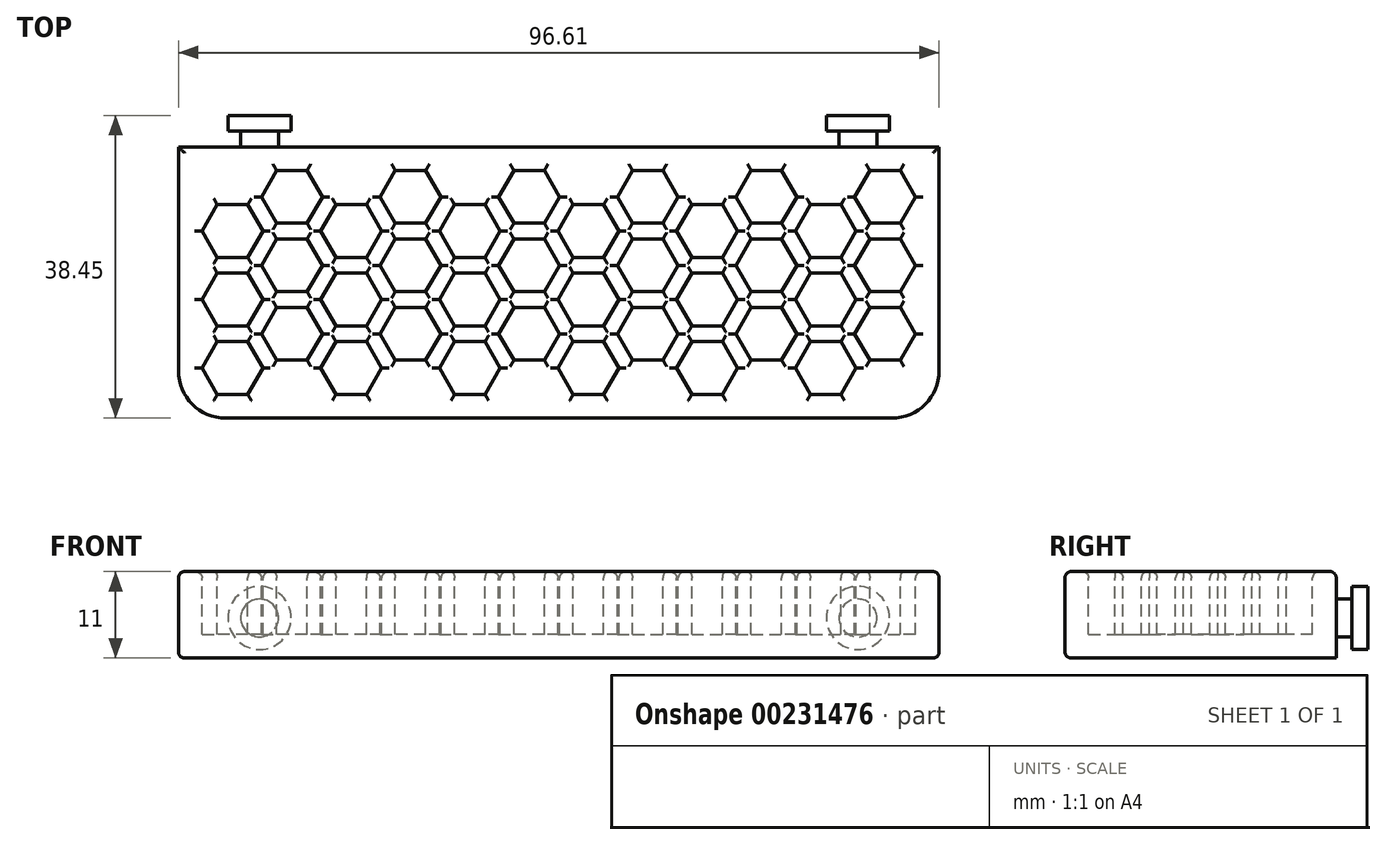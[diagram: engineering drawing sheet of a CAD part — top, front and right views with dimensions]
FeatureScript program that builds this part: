
annotation { "Feature Type Name" : "Feature", "Feature Type Description" : "" }
export const myFeature = defineFeature(function(context is Context, id is Id, definition is map)
    precondition{}
    {
        {
            var Q0;
            Q0=qCreatedBy(makeId("Top.planeOp"),FACE);
            var sketch = newSketch(context, id + "F0", { "sketchPlane" : qUnion([Q0])});
            skCircle(sketch, "E0.cCircle", {"center": v(0, 0) * mm, "radius": 3.35 * mm, "construction": true});
            skLineSegment(sketch, "E0.0", {"start": v(1.93, -3.35) * mm, "end": v(-1.93, -3.35) * mm, "construction": true});
            skLineSegment(sketch, "E0.1", {"start": v(-1.93, -3.35) * mm, "end": v(-3.87, 0) * mm, "construction": true});
            skLineSegment(sketch, "E0.2", {"start": v(-3.87, 0) * mm, "end": v(-1.93, 3.35) * mm, "construction": true});
            skLineSegment(sketch, "E0.3", {"start": v(-1.93, 3.35) * mm, "end": v(1.93, 3.35) * mm, "construction": true});
            skLineSegment(sketch, "E0.4", {"start": v(1.93, 3.35) * mm, "end": v(3.87, 0) * mm, "construction": true});
            skLineSegment(sketch, "E0.5", {"start": v(3.87, 0) * mm, "end": v(1.93, -3.35) * mm, "construction": true});
            skPoint(sketch, "E0.0.midPoint", {"position": v(0, -3.35) * mm});
            skLineSegment(sketch, "E1", {"start": v(1.18, 6.66) * mm, "end": v(5.6, -1) * mm, "construction": true});
            skPoint(sketch, "E2", {"position": v(7.53, 4.35) * mm});
            skCircle(sketch, "E3.0.1.0", {"center": v(7.53, 4.35) * mm, "radius": 3.35 * mm, "construction": true});
            skLineSegment(sketch, "E3.0.1.1", {"start": v(3.67, 4.35) * mm, "end": v(5.6, 7.7) * mm, "construction": true});
            skLineSegment(sketch, "E3.0.1.2", {"start": v(9.47, 7.7) * mm, "end": v(11.4, 4.35) * mm, "construction": true});
            skLineSegment(sketch, "E3.0.1.3", {"start": v(11.4, 4.35) * mm, "end": v(9.47, 1) * mm, "construction": true});
            skPoint(sketch, "E3.0.1.4", {"position": v(7.53, 1) * mm});
            skLineSegment(sketch, "E3.0.1.5", {"start": v(5.6, 1) * mm, "end": v(3.67, 4.35) * mm, "construction": true});
            skLineSegment(sketch, "E3.0.1.6", {"start": v(9.47, 1) * mm, "end": v(5.6, 1) * mm, "construction": true});
            skLineSegment(sketch, "E3.0.1.7", {"start": v(5.6, 7.7) * mm, "end": v(9.47, 7.7) * mm, "construction": true});
            skCircle(sketch, "E3.0.2.0", {"center": v(15.07, 8.7) * mm, "radius": 3.35 * mm, "construction": true});
            skLineSegment(sketch, "E3.0.2.1", {"start": v(11.2, 8.7) * mm, "end": v(13.13, 12.05) * mm, "construction": true});
            skLineSegment(sketch, "E3.0.2.2", {"start": v(17, 12.05) * mm, "end": v(18.94, 8.7) * mm, "construction": true});
            skLineSegment(sketch, "E3.0.2.3", {"start": v(18.94, 8.7) * mm, "end": v(17, 5.35) * mm, "construction": true});
            skPoint(sketch, "E3.0.2.4", {"position": v(15.07, 5.35) * mm});
            skLineSegment(sketch, "E3.0.2.5", {"start": v(13.13, 5.35) * mm, "end": v(11.2, 8.7) * mm, "construction": true});
            skLineSegment(sketch, "E3.0.2.6", {"start": v(17, 5.35) * mm, "end": v(13.13, 5.35) * mm, "construction": true});
            skLineSegment(sketch, "E3.0.2.7", {"start": v(13.13, 12.05) * mm, "end": v(17, 12.05) * mm, "construction": true});
            skCircle(sketch, "E3.1.0.0", {"center": v(15.07, 0) * mm, "radius": 3.35 * mm, "construction": true});
            skLineSegment(sketch, "E3.1.0.1", {"start": v(11.2, 0) * mm, "end": v(13.13, 3.35) * mm, "construction": true});
            skLineSegment(sketch, "E3.1.0.2", {"start": v(17, 3.35) * mm, "end": v(18.94, 0) * mm, "construction": true});
            skLineSegment(sketch, "E3.1.0.3", {"start": v(18.94, 0) * mm, "end": v(17, -3.35) * mm, "construction": true});
            skPoint(sketch, "E3.1.0.4", {"position": v(15.07, -3.35) * mm});
            skLineSegment(sketch, "E3.1.0.5", {"start": v(13.13, -3.35) * mm, "end": v(11.2, 0) * mm, "construction": true});
            skLineSegment(sketch, "E3.1.0.6", {"start": v(17, -3.35) * mm, "end": v(13.13, -3.35) * mm, "construction": true});
            skLineSegment(sketch, "E3.1.0.7", {"start": v(13.13, 3.35) * mm, "end": v(17, 3.35) * mm, "construction": true});
            skCircle(sketch, "E3.1.1.0", {"center": v(22.6, 4.35) * mm, "radius": 3.35 * mm, "construction": true});
            skLineSegment(sketch, "E3.1.1.1", {"start": v(18.74, 4.35) * mm, "end": v(20.67, 7.7) * mm, "construction": true});
            skLineSegment(sketch, "E3.1.1.2", {"start": v(24.54, 7.7) * mm, "end": v(26.47, 4.35) * mm});
            skLineSegment(sketch, "E3.1.1.3", {"start": v(26.47, 4.35) * mm, "end": v(24.54, 1) * mm, "construction": true});
            skPoint(sketch, "E3.1.1.4", {"position": v(22.6, 1) * mm});
            skLineSegment(sketch, "E3.1.1.5", {"start": v(20.67, 1) * mm, "end": v(18.74, 4.35) * mm, "construction": true});
            skLineSegment(sketch, "E3.1.1.6", {"start": v(24.54, 1) * mm, "end": v(20.67, 1) * mm, "construction": true});
            skLineSegment(sketch, "E3.1.1.7", {"start": v(20.67, 7.7) * mm, "end": v(24.54, 7.7) * mm, "construction": true});
            skCircle(sketch, "E3.1.2.0", {"center": v(30.14, 8.7) * mm, "radius": 3.35 * mm, "construction": true});
            skLineSegment(sketch, "E3.1.2.1", {"start": v(26.27, 8.7) * mm, "end": v(28.2, 12.05) * mm});
            skLineSegment(sketch, "E3.1.2.2", {"start": v(32.07, 12.05) * mm, "end": v(34, 8.7) * mm});
            skLineSegment(sketch, "E3.1.2.3", {"start": v(34, 8.7) * mm, "end": v(32.07, 5.35) * mm});
            skPoint(sketch, "E3.1.2.4", {"position": v(30.14, 5.35) * mm});
            skLineSegment(sketch, "E3.1.2.5", {"start": v(28.2, 5.35) * mm, "end": v(26.27, 8.7) * mm});
            skLineSegment(sketch, "E3.1.2.6", {"start": v(32.07, 5.35) * mm, "end": v(28.2, 5.35) * mm});
            skLineSegment(sketch, "E3.1.2.7", {"start": v(28.2, 12.05) * mm, "end": v(32.07, 12.05) * mm});
            skCircle(sketch, "E3.2.0.0", {"center": v(30.14, 0) * mm, "radius": 3.35 * mm, "construction": true});
            skLineSegment(sketch, "E3.2.0.1", {"start": v(26.27, 0) * mm, "end": v(28.2, 3.35) * mm});
            skLineSegment(sketch, "E3.2.0.2", {"start": v(32.07, 3.35) * mm, "end": v(34, 0) * mm});
            skLineSegment(sketch, "E3.2.0.3", {"start": v(34, 0) * mm, "end": v(32.07, -3.35) * mm});
            skPoint(sketch, "E3.2.0.4", {"position": v(30.14, -3.35) * mm});
            skLineSegment(sketch, "E3.2.0.5", {"start": v(28.2, -3.35) * mm, "end": v(26.27, 0) * mm});
            skLineSegment(sketch, "E3.2.0.6", {"start": v(32.07, -3.35) * mm, "end": v(28.2, -3.35) * mm});
            skLineSegment(sketch, "E3.2.0.7", {"start": v(28.2, 3.35) * mm, "end": v(32.07, 3.35) * mm});
            skCircle(sketch, "E3.2.1.0", {"center": v(37.67, 4.35) * mm, "radius": 3.35 * mm, "construction": true});
            skLineSegment(sketch, "E3.2.1.1", {"start": v(33.8, 4.35) * mm, "end": v(35.74, 7.7) * mm});
            skLineSegment(sketch, "E3.2.1.2", {"start": v(39.6, 7.7) * mm, "end": v(41.54, 4.35) * mm});
            skLineSegment(sketch, "E3.2.1.3", {"start": v(41.54, 4.35) * mm, "end": v(39.6, 1) * mm});
            skPoint(sketch, "E3.2.1.4", {"position": v(37.67, 1) * mm});
            skLineSegment(sketch, "E3.2.1.5", {"start": v(35.74, 1) * mm, "end": v(33.8, 4.35) * mm});
            skLineSegment(sketch, "E3.2.1.6", {"start": v(39.6, 1) * mm, "end": v(35.74, 1) * mm});
            skLineSegment(sketch, "E3.2.1.7", {"start": v(35.74, 7.7) * mm, "end": v(39.6, 7.7) * mm});
            skCircle(sketch, "E3.2.2.0", {"center": v(45.2, 8.7) * mm, "radius": 3.35 * mm, "construction": true});
            skLineSegment(sketch, "E3.2.2.1", {"start": v(41.34, 8.7) * mm, "end": v(43.27, 12.05) * mm});
            skLineSegment(sketch, "E3.2.2.2", {"start": v(47.14, 12.05) * mm, "end": v(49.07, 8.7) * mm});
            skLineSegment(sketch, "E3.2.2.3", {"start": v(49.07, 8.7) * mm, "end": v(47.14, 5.35) * mm});
            skPoint(sketch, "E3.2.2.4", {"position": v(45.2, 5.35) * mm});
            skLineSegment(sketch, "E3.2.2.5", {"start": v(43.27, 5.35) * mm, "end": v(41.34, 8.7) * mm});
            skLineSegment(sketch, "E3.2.2.6", {"start": v(47.14, 5.35) * mm, "end": v(43.27, 5.35) * mm});
            skLineSegment(sketch, "E3.2.2.7", {"start": v(43.27, 12.05) * mm, "end": v(47.14, 12.05) * mm});
            skCircle(sketch, "E3.3.0.0", {"center": v(45.2, 0) * mm, "radius": 3.35 * mm, "construction": true});
            skLineSegment(sketch, "E3.3.0.1", {"start": v(41.34, 0) * mm, "end": v(43.27, 3.35) * mm});
            skLineSegment(sketch, "E3.3.0.2", {"start": v(47.14, 3.35) * mm, "end": v(49.07, 0) * mm});
            skLineSegment(sketch, "E3.3.0.3", {"start": v(49.07, 0) * mm, "end": v(47.14, -3.35) * mm});
            skPoint(sketch, "E3.3.0.4", {"position": v(45.2, -3.35) * mm});
            skLineSegment(sketch, "E3.3.0.5", {"start": v(43.27, -3.35) * mm, "end": v(41.34, 0) * mm});
            skLineSegment(sketch, "E3.3.0.6", {"start": v(47.14, -3.35) * mm, "end": v(43.27, -3.35) * mm});
            skLineSegment(sketch, "E3.3.0.7", {"start": v(43.27, 3.35) * mm, "end": v(47.14, 3.35) * mm});
            skCircle(sketch, "E3.3.1.0", {"center": v(52.74, 4.35) * mm, "radius": 3.35 * mm, "construction": true});
            skLineSegment(sketch, "E3.3.1.1", {"start": v(48.87, 4.35) * mm, "end": v(50.8, 7.7) * mm});
            skLineSegment(sketch, "E3.3.1.2", {"start": v(54.68, 7.7) * mm, "end": v(56.6, 4.35) * mm});
            skLineSegment(sketch, "E3.3.1.3", {"start": v(56.6, 4.35) * mm, "end": v(54.68, 1) * mm});
            skPoint(sketch, "E3.3.1.4", {"position": v(52.74, 1) * mm});
            skLineSegment(sketch, "E3.3.1.5", {"start": v(50.8, 1) * mm, "end": v(48.87, 4.35) * mm});
            skLineSegment(sketch, "E3.3.1.6", {"start": v(54.68, 1) * mm, "end": v(50.8, 1) * mm});
            skLineSegment(sketch, "E3.3.1.7", {"start": v(50.8, 7.7) * mm, "end": v(54.68, 7.7) * mm});
            skCircle(sketch, "E3.3.2.0", {"center": v(60.28, 8.7) * mm, "radius": 3.35 * mm, "construction": true});
            skLineSegment(sketch, "E3.3.2.1", {"start": v(56.4, 8.7) * mm, "end": v(58.34, 12.05) * mm});
            skLineSegment(sketch, "E3.3.2.2", {"start": v(62.2, 12.05) * mm, "end": v(64.14, 8.7) * mm});
            skLineSegment(sketch, "E3.3.2.3", {"start": v(64.14, 8.7) * mm, "end": v(62.2, 5.35) * mm});
            skPoint(sketch, "E3.3.2.4", {"position": v(60.28, 5.35) * mm});
            skLineSegment(sketch, "E3.3.2.5", {"start": v(58.34, 5.35) * mm, "end": v(56.4, 8.7) * mm});
            skLineSegment(sketch, "E3.3.2.6", {"start": v(62.2, 5.35) * mm, "end": v(58.34, 5.35) * mm});
            skLineSegment(sketch, "E3.3.2.7", {"start": v(58.34, 12.05) * mm, "end": v(62.2, 12.05) * mm});
            skCircle(sketch, "E3.4.0.0", {"center": v(60.28, 0) * mm, "radius": 3.35 * mm, "construction": true});
            skLineSegment(sketch, "E3.4.0.1", {"start": v(56.4, 0) * mm, "end": v(58.34, 3.35) * mm});
            skLineSegment(sketch, "E3.4.0.2", {"start": v(62.2, 3.35) * mm, "end": v(64.14, 0) * mm});
            skLineSegment(sketch, "E3.4.0.3", {"start": v(64.14, 0) * mm, "end": v(62.2, -3.35) * mm});
            skPoint(sketch, "E3.4.0.4", {"position": v(60.28, -3.35) * mm});
            skLineSegment(sketch, "E3.4.0.5", {"start": v(58.34, -3.35) * mm, "end": v(56.4, 0) * mm});
            skLineSegment(sketch, "E3.4.0.6", {"start": v(62.2, -3.35) * mm, "end": v(58.34, -3.35) * mm});
            skLineSegment(sketch, "E3.4.0.7", {"start": v(58.34, 3.35) * mm, "end": v(62.2, 3.35) * mm});
            skCircle(sketch, "E3.4.1.0", {"center": v(67.8, 4.35) * mm, "radius": 3.35 * mm, "construction": true});
            skLineSegment(sketch, "E3.4.1.1", {"start": v(63.94, 4.35) * mm, "end": v(65.88, 7.7) * mm});
            skLineSegment(sketch, "E3.4.1.2", {"start": v(69.74, 7.7) * mm, "end": v(71.68, 4.35) * mm});
            skLineSegment(sketch, "E3.4.1.3", {"start": v(71.68, 4.35) * mm, "end": v(69.74, 1) * mm});
            skPoint(sketch, "E3.4.1.4", {"position": v(67.8, 1) * mm});
            skLineSegment(sketch, "E3.4.1.5", {"start": v(65.88, 1) * mm, "end": v(63.94, 4.35) * mm});
            skLineSegment(sketch, "E3.4.1.6", {"start": v(69.74, 1) * mm, "end": v(65.88, 1) * mm});
            skLineSegment(sketch, "E3.4.1.7", {"start": v(65.88, 7.7) * mm, "end": v(69.74, 7.7) * mm});
            skCircle(sketch, "E3.4.2.0", {"center": v(75.34, 8.7) * mm, "radius": 3.35 * mm, "construction": true});
            skLineSegment(sketch, "E3.4.2.1", {"start": v(71.48, 8.7) * mm, "end": v(73.41, 12.05) * mm});
            skLineSegment(sketch, "E3.4.2.2", {"start": v(77.28, 12.05) * mm, "end": v(79.21, 8.7) * mm});
            skLineSegment(sketch, "E3.4.2.3", {"start": v(79.21, 8.7) * mm, "end": v(77.28, 5.35) * mm});
            skPoint(sketch, "E3.4.2.4", {"position": v(75.34, 5.35) * mm});
            skLineSegment(sketch, "E3.4.2.5", {"start": v(73.41, 5.35) * mm, "end": v(71.48, 8.7) * mm});
            skLineSegment(sketch, "E3.4.2.6", {"start": v(77.28, 5.35) * mm, "end": v(73.41, 5.35) * mm});
            skLineSegment(sketch, "E3.4.2.7", {"start": v(73.41, 12.05) * mm, "end": v(77.28, 12.05) * mm});
            skCircle(sketch, "E3.5.0.0", {"center": v(75.34, 0) * mm, "radius": 3.35 * mm, "construction": true});
            skLineSegment(sketch, "E3.5.0.1", {"start": v(71.48, 0) * mm, "end": v(73.41, 3.35) * mm});
            skLineSegment(sketch, "E3.5.0.2", {"start": v(77.28, 3.35) * mm, "end": v(79.21, 0) * mm});
            skLineSegment(sketch, "E3.5.0.3", {"start": v(79.21, 0) * mm, "end": v(77.28, -3.35) * mm});
            skPoint(sketch, "E3.5.0.4", {"position": v(75.34, -3.35) * mm});
            skLineSegment(sketch, "E3.5.0.5", {"start": v(73.41, -3.35) * mm, "end": v(71.48, 0) * mm});
            skLineSegment(sketch, "E3.5.0.6", {"start": v(77.28, -3.35) * mm, "end": v(73.41, -3.35) * mm});
            skLineSegment(sketch, "E3.5.0.7", {"start": v(73.41, 3.35) * mm, "end": v(77.28, 3.35) * mm});
            skCircle(sketch, "E3.5.1.0", {"center": v(82.88, 4.35) * mm, "radius": 3.35 * mm});
            skLineSegment(sketch, "E3.5.1.1", {"start": v(79.01, 4.35) * mm, "end": v(80.94, 7.7) * mm});
            skLineSegment(sketch, "E3.5.1.2", {"start": v(84.81, 7.7) * mm, "end": v(86.75, 4.35) * mm});
            skLineSegment(sketch, "E3.5.1.3", {"start": v(86.75, 4.35) * mm, "end": v(84.81, 1) * mm});
            skPoint(sketch, "E3.5.1.4", {"position": v(82.88, 1) * mm});
            skLineSegment(sketch, "E3.5.1.5", {"start": v(80.94, 1) * mm, "end": v(79.01, 4.35) * mm});
            skLineSegment(sketch, "E3.5.1.6", {"start": v(84.81, 1) * mm, "end": v(80.94, 1) * mm});
            skLineSegment(sketch, "E3.5.1.7", {"start": v(80.94, 7.7) * mm, "end": v(84.81, 7.7) * mm});
            skCircle(sketch, "E3.5.2.0", {"center": v(90.41, 8.7) * mm, "radius": 3.35 * mm});
            skLineSegment(sketch, "E3.5.2.1", {"start": v(86.54, 8.7) * mm, "end": v(88.48, 12.05) * mm});
            skLineSegment(sketch, "E3.5.2.2", {"start": v(92.35, 12.05) * mm, "end": v(94.28, 8.7) * mm});
            skLineSegment(sketch, "E3.5.2.3", {"start": v(94.28, 8.7) * mm, "end": v(92.35, 5.35) * mm});
            skPoint(sketch, "E3.5.2.4", {"position": v(90.41, 5.35) * mm});
            skLineSegment(sketch, "E3.5.2.5", {"start": v(88.48, 5.35) * mm, "end": v(86.54, 8.7) * mm});
            skLineSegment(sketch, "E3.5.2.6", {"start": v(92.35, 5.35) * mm, "end": v(88.48, 5.35) * mm});
            skLineSegment(sketch, "E3.5.2.7", {"start": v(88.48, 12.05) * mm, "end": v(92.35, 12.05) * mm});
            skLineSegment(sketch, "E3.direction1", {"start": v(-1.93, -3.35) * mm, "end": v(13.13, -3.35) * mm, "construction": true});
            skLineSegment(sketch, "E3.direction2", {"start": v(-1.93, -3.35) * mm, "end": v(5.6, 1) * mm, "construction": true});
            skLineSegment(sketch, "E4", {"start": v(12.67, 4.55) * mm, "end": v(9.71, -0.58) * mm, "construction": true});
            skCircle(sketch, "E5.0.0.3", {"center": v(22.6, 13.05) * mm, "radius": 3.35 * mm, "construction": true});
            skLineSegment(sketch, "E5.2.0.3", {"start": v(18.74, 13.05) * mm, "end": v(20.67, 16.4) * mm, "construction": true});
            skLineSegment(sketch, "E5.5.0.3", {"start": v(24.54, 16.4) * mm, "end": v(26.47, 13.05) * mm, "construction": true});
            skLineSegment(sketch, "E5.8.0.3", {"start": v(26.47, 13.05) * mm, "end": v(24.54, 9.7) * mm, "construction": true});
            skPoint(sketch, "E5.11.0.3", {"position": v(22.6, 9.7) * mm});
            skLineSegment(sketch, "E5.12.0.3", {"start": v(20.67, 9.7) * mm, "end": v(18.74, 13.05) * mm, "construction": true});
            skLineSegment(sketch, "E5.15.0.3", {"start": v(24.54, 9.7) * mm, "end": v(20.67, 9.7) * mm, "construction": true});
            skLineSegment(sketch, "E5.18.0.3", {"start": v(20.67, 16.4) * mm, "end": v(24.54, 16.4) * mm, "construction": true});
            skCircle(sketch, "E5.0.1.3", {"center": v(37.67, 13.05) * mm, "radius": 3.35 * mm, "construction": true});
            skLineSegment(sketch, "E5.2.1.3", {"start": v(33.8, 13.05) * mm, "end": v(35.74, 16.4) * mm});
            skLineSegment(sketch, "E5.5.1.3", {"start": v(39.6, 16.4) * mm, "end": v(41.54, 13.05) * mm});
            skLineSegment(sketch, "E5.8.1.3", {"start": v(41.54, 13.05) * mm, "end": v(39.6, 9.7) * mm});
            skPoint(sketch, "E5.11.1.3", {"position": v(37.67, 9.7) * mm});
            skLineSegment(sketch, "E5.12.1.3", {"start": v(35.74, 9.7) * mm, "end": v(33.8, 13.05) * mm});
            skLineSegment(sketch, "E5.15.1.3", {"start": v(39.6, 9.7) * mm, "end": v(35.74, 9.7) * mm});
            skLineSegment(sketch, "E5.18.1.3", {"start": v(35.74, 16.4) * mm, "end": v(39.6, 16.4) * mm});
            skCircle(sketch, "E5.0.2.3", {"center": v(52.74, 13.05) * mm, "radius": 3.35 * mm, "construction": true});
            skLineSegment(sketch, "E5.2.2.3", {"start": v(48.87, 13.05) * mm, "end": v(50.8, 16.4) * mm});
            skLineSegment(sketch, "E5.5.2.3", {"start": v(54.68, 16.4) * mm, "end": v(56.6, 13.05) * mm});
            skLineSegment(sketch, "E5.8.2.3", {"start": v(56.6, 13.05) * mm, "end": v(54.68, 9.7) * mm});
            skPoint(sketch, "E5.11.2.3", {"position": v(52.74, 9.7) * mm});
            skLineSegment(sketch, "E5.12.2.3", {"start": v(50.8, 9.7) * mm, "end": v(48.87, 13.05) * mm});
            skLineSegment(sketch, "E5.15.2.3", {"start": v(54.68, 9.7) * mm, "end": v(50.8, 9.7) * mm});
            skLineSegment(sketch, "E5.18.2.3", {"start": v(50.8, 16.4) * mm, "end": v(54.68, 16.4) * mm});
            skCircle(sketch, "E5.0.3.3", {"center": v(67.8, 13.05) * mm, "radius": 3.35 * mm, "construction": true});
            skLineSegment(sketch, "E5.2.3.3", {"start": v(63.94, 13.05) * mm, "end": v(65.88, 16.4) * mm});
            skLineSegment(sketch, "E5.5.3.3", {"start": v(69.74, 16.4) * mm, "end": v(71.68, 13.05) * mm});
            skLineSegment(sketch, "E5.8.3.3", {"start": v(71.68, 13.05) * mm, "end": v(69.74, 9.7) * mm});
            skPoint(sketch, "E5.11.3.3", {"position": v(67.8, 9.7) * mm});
            skLineSegment(sketch, "E5.12.3.3", {"start": v(65.88, 9.7) * mm, "end": v(63.94, 13.05) * mm});
            skLineSegment(sketch, "E5.15.3.3", {"start": v(69.74, 9.7) * mm, "end": v(65.88, 9.7) * mm});
            skLineSegment(sketch, "E5.18.3.3", {"start": v(65.88, 16.4) * mm, "end": v(69.74, 16.4) * mm});
            skCircle(sketch, "E5.0.4.3", {"center": v(82.88, 13.05) * mm, "radius": 3.35 * mm});
            skLineSegment(sketch, "E5.2.4.3", {"start": v(79.01, 13.05) * mm, "end": v(80.94, 16.4) * mm});
            skLineSegment(sketch, "E5.5.4.3", {"start": v(84.81, 16.4) * mm, "end": v(86.75, 13.05) * mm});
            skLineSegment(sketch, "E5.8.4.3", {"start": v(86.75, 13.05) * mm, "end": v(84.81, 9.7) * mm});
            skPoint(sketch, "E5.11.4.3", {"position": v(82.88, 9.7) * mm});
            skLineSegment(sketch, "E5.12.4.3", {"start": v(80.94, 9.7) * mm, "end": v(79.01, 13.05) * mm});
            skLineSegment(sketch, "E5.15.4.3", {"start": v(84.81, 9.7) * mm, "end": v(80.94, 9.7) * mm});
            skLineSegment(sketch, "E5.18.4.3", {"start": v(80.94, 16.4) * mm, "end": v(84.81, 16.4) * mm});
            skCircle(sketch, "E5.0.5.3", {"center": v(97.95, 13.05) * mm, "radius": 3.35 * mm});
            skLineSegment(sketch, "E5.2.5.3", {"start": v(94.08, 13.05) * mm, "end": v(96.01, 16.4) * mm});
            skLineSegment(sketch, "E5.5.5.3", {"start": v(99.88, 16.4) * mm, "end": v(101.82, 13.05) * mm});
            skLineSegment(sketch, "E5.8.5.3", {"start": v(101.82, 13.05) * mm, "end": v(99.88, 9.7) * mm});
            skPoint(sketch, "E5.11.5.3", {"position": v(97.95, 9.7) * mm});
            skLineSegment(sketch, "E5.12.5.3", {"start": v(96.01, 9.7) * mm, "end": v(94.08, 13.05) * mm});
            skLineSegment(sketch, "E5.15.5.3", {"start": v(99.88, 9.7) * mm, "end": v(96.01, 9.7) * mm});
            skLineSegment(sketch, "E5.18.5.3", {"start": v(96.01, 16.4) * mm, "end": v(99.88, 16.4) * mm});
            skCircle(sketch, "E6.0.0.4", {"center": v(30.14, 17.4) * mm, "radius": 3.35 * mm, "construction": true});
            skLineSegment(sketch, "E6.2.0.4", {"start": v(26.27, 17.4) * mm, "end": v(28.2, 20.75) * mm});
            skLineSegment(sketch, "E6.5.0.4", {"start": v(32.07, 20.75) * mm, "end": v(34, 17.4) * mm});
            skLineSegment(sketch, "E6.8.0.4", {"start": v(34, 17.4) * mm, "end": v(32.07, 14.05) * mm});
            skPoint(sketch, "E6.11.0.4", {"position": v(30.14, 14.05) * mm});
            skLineSegment(sketch, "E6.12.0.4", {"start": v(28.2, 14.05) * mm, "end": v(26.27, 17.4) * mm});
            skLineSegment(sketch, "E6.15.0.4", {"start": v(32.07, 14.05) * mm, "end": v(28.2, 14.05) * mm});
            skLineSegment(sketch, "E6.18.0.4", {"start": v(28.2, 20.75) * mm, "end": v(32.07, 20.75) * mm});
            skCircle(sketch, "E6.0.0.5", {"center": v(37.67, 21.75) * mm, "radius": 3.35 * mm, "construction": true});
            skLineSegment(sketch, "E6.2.0.5", {"start": v(33.8, 21.75) * mm, "end": v(35.74, 25.1) * mm});
            skLineSegment(sketch, "E6.5.0.5", {"start": v(39.6, 25.1) * mm, "end": v(41.54, 21.75) * mm});
            skLineSegment(sketch, "E6.8.0.5", {"start": v(41.54, 21.75) * mm, "end": v(39.6, 18.4) * mm});
            skPoint(sketch, "E6.11.0.5", {"position": v(37.67, 18.4) * mm});
            skLineSegment(sketch, "E6.12.0.5", {"start": v(35.74, 18.4) * mm, "end": v(33.8, 21.75) * mm});
            skLineSegment(sketch, "E6.15.0.5", {"start": v(39.6, 18.4) * mm, "end": v(35.74, 18.4) * mm});
            skLineSegment(sketch, "E6.18.0.5", {"start": v(35.74, 25.1) * mm, "end": v(39.6, 25.1) * mm});
            skCircle(sketch, "E6.0.1.4", {"center": v(45.2, 17.4) * mm, "radius": 3.35 * mm, "construction": true});
            skLineSegment(sketch, "E6.2.1.4", {"start": v(41.34, 17.4) * mm, "end": v(43.27, 20.75) * mm});
            skLineSegment(sketch, "E6.5.1.4", {"start": v(47.14, 20.75) * mm, "end": v(49.07, 17.4) * mm});
            skLineSegment(sketch, "E6.8.1.4", {"start": v(49.07, 17.4) * mm, "end": v(47.14, 14.05) * mm});
            skPoint(sketch, "E6.11.1.4", {"position": v(45.2, 14.05) * mm});
            skLineSegment(sketch, "E6.12.1.4", {"start": v(43.27, 14.05) * mm, "end": v(41.34, 17.4) * mm});
            skLineSegment(sketch, "E6.15.1.4", {"start": v(47.14, 14.05) * mm, "end": v(43.27, 14.05) * mm});
            skLineSegment(sketch, "E6.18.1.4", {"start": v(43.27, 20.75) * mm, "end": v(47.14, 20.75) * mm});
            skCircle(sketch, "E6.0.1.5", {"center": v(52.74, 21.75) * mm, "radius": 3.35 * mm, "construction": true});
            skLineSegment(sketch, "E6.2.1.5", {"start": v(48.87, 21.75) * mm, "end": v(50.8, 25.1) * mm});
            skLineSegment(sketch, "E6.5.1.5", {"start": v(54.68, 25.1) * mm, "end": v(56.6, 21.75) * mm});
            skLineSegment(sketch, "E6.8.1.5", {"start": v(56.6, 21.75) * mm, "end": v(54.68, 18.4) * mm});
            skPoint(sketch, "E6.11.1.5", {"position": v(52.74, 18.4) * mm});
            skLineSegment(sketch, "E6.12.1.5", {"start": v(50.8, 18.4) * mm, "end": v(48.87, 21.75) * mm});
            skLineSegment(sketch, "E6.15.1.5", {"start": v(54.68, 18.4) * mm, "end": v(50.8, 18.4) * mm});
            skLineSegment(sketch, "E6.18.1.5", {"start": v(50.8, 25.1) * mm, "end": v(54.68, 25.1) * mm});
            skCircle(sketch, "E6.0.2.4", {"center": v(60.28, 17.4) * mm, "radius": 3.35 * mm, "construction": true});
            skLineSegment(sketch, "E6.2.2.4", {"start": v(56.4, 17.4) * mm, "end": v(58.34, 20.75) * mm});
            skLineSegment(sketch, "E6.5.2.4", {"start": v(62.2, 20.75) * mm, "end": v(64.14, 17.4) * mm});
            skLineSegment(sketch, "E6.8.2.4", {"start": v(64.14, 17.4) * mm, "end": v(62.2, 14.05) * mm});
            skPoint(sketch, "E6.11.2.4", {"position": v(60.28, 14.05) * mm});
            skLineSegment(sketch, "E6.12.2.4", {"start": v(58.34, 14.05) * mm, "end": v(56.4, 17.4) * mm});
            skLineSegment(sketch, "E6.15.2.4", {"start": v(62.2, 14.05) * mm, "end": v(58.34, 14.05) * mm});
            skLineSegment(sketch, "E6.18.2.4", {"start": v(58.34, 20.75) * mm, "end": v(62.2, 20.75) * mm});
            skCircle(sketch, "E6.0.2.5", {"center": v(67.8, 21.75) * mm, "radius": 3.35 * mm, "construction": true});
            skLineSegment(sketch, "E6.2.2.5", {"start": v(63.94, 21.75) * mm, "end": v(65.88, 25.1) * mm});
            skLineSegment(sketch, "E6.5.2.5", {"start": v(69.74, 25.1) * mm, "end": v(71.68, 21.75) * mm});
            skLineSegment(sketch, "E6.8.2.5", {"start": v(71.68, 21.75) * mm, "end": v(69.74, 18.4) * mm});
            skPoint(sketch, "E6.11.2.5", {"position": v(67.8, 18.4) * mm});
            skLineSegment(sketch, "E6.12.2.5", {"start": v(65.88, 18.4) * mm, "end": v(63.94, 21.75) * mm});
            skLineSegment(sketch, "E6.15.2.5", {"start": v(69.74, 18.4) * mm, "end": v(65.88, 18.4) * mm});
            skLineSegment(sketch, "E6.18.2.5", {"start": v(65.88, 25.1) * mm, "end": v(69.74, 25.1) * mm});
            skCircle(sketch, "E6.0.3.4", {"center": v(75.34, 17.4) * mm, "radius": 3.35 * mm, "construction": true});
            skLineSegment(sketch, "E6.2.3.4", {"start": v(71.48, 17.4) * mm, "end": v(73.41, 20.75) * mm});
            skLineSegment(sketch, "E6.5.3.4", {"start": v(77.28, 20.75) * mm, "end": v(79.21, 17.4) * mm});
            skLineSegment(sketch, "E6.8.3.4", {"start": v(79.21, 17.4) * mm, "end": v(77.28, 14.05) * mm});
            skPoint(sketch, "E6.11.3.4", {"position": v(75.34, 14.05) * mm});
            skLineSegment(sketch, "E6.12.3.4", {"start": v(73.41, 14.05) * mm, "end": v(71.48, 17.4) * mm});
            skLineSegment(sketch, "E6.15.3.4", {"start": v(77.28, 14.05) * mm, "end": v(73.41, 14.05) * mm});
            skLineSegment(sketch, "E6.18.3.4", {"start": v(73.41, 20.75) * mm, "end": v(77.28, 20.75) * mm});
            skCircle(sketch, "E6.0.3.5", {"center": v(82.88, 21.75) * mm, "radius": 3.35 * mm});
            skLineSegment(sketch, "E6.2.3.5", {"start": v(79.01, 21.75) * mm, "end": v(80.94, 25.1) * mm});
            skLineSegment(sketch, "E6.5.3.5", {"start": v(84.81, 25.1) * mm, "end": v(86.75, 21.75) * mm});
            skLineSegment(sketch, "E6.8.3.5", {"start": v(86.75, 21.75) * mm, "end": v(84.81, 18.4) * mm});
            skPoint(sketch, "E6.11.3.5", {"position": v(82.88, 18.4) * mm});
            skLineSegment(sketch, "E6.12.3.5", {"start": v(80.94, 18.4) * mm, "end": v(79.01, 21.75) * mm});
            skLineSegment(sketch, "E6.15.3.5", {"start": v(84.81, 18.4) * mm, "end": v(80.94, 18.4) * mm});
            skLineSegment(sketch, "E6.18.3.5", {"start": v(80.94, 25.1) * mm, "end": v(84.81, 25.1) * mm});
            skCircle(sketch, "E6.0.4.4", {"center": v(90.41, 17.4) * mm, "radius": 3.35 * mm});
            skLineSegment(sketch, "E6.2.4.4", {"start": v(86.54, 17.4) * mm, "end": v(88.48, 20.75) * mm});
            skLineSegment(sketch, "E6.5.4.4", {"start": v(92.35, 20.75) * mm, "end": v(94.28, 17.4) * mm});
            skLineSegment(sketch, "E6.8.4.4", {"start": v(94.28, 17.4) * mm, "end": v(92.35, 14.05) * mm});
            skPoint(sketch, "E6.11.4.4", {"position": v(90.41, 14.05) * mm});
            skLineSegment(sketch, "E6.12.4.4", {"start": v(88.48, 14.05) * mm, "end": v(86.54, 17.4) * mm});
            skLineSegment(sketch, "E6.15.4.4", {"start": v(92.35, 14.05) * mm, "end": v(88.48, 14.05) * mm});
            skLineSegment(sketch, "E6.18.4.4", {"start": v(88.48, 20.75) * mm, "end": v(92.35, 20.75) * mm});
            skCircle(sketch, "E6.0.4.5", {"center": v(97.95, 21.75) * mm, "radius": 3.35 * mm});
            skLineSegment(sketch, "E6.2.4.5", {"start": v(94.08, 21.75) * mm, "end": v(96.01, 25.1) * mm});
            skLineSegment(sketch, "E6.5.4.5", {"start": v(99.88, 25.1) * mm, "end": v(101.82, 21.75) * mm});
            skLineSegment(sketch, "E6.8.4.5", {"start": v(101.82, 21.75) * mm, "end": v(99.88, 18.4) * mm});
            skPoint(sketch, "E6.11.4.5", {"position": v(97.95, 18.4) * mm});
            skLineSegment(sketch, "E6.12.4.5", {"start": v(96.01, 18.4) * mm, "end": v(94.08, 21.75) * mm});
            skLineSegment(sketch, "E6.15.4.5", {"start": v(99.88, 18.4) * mm, "end": v(96.01, 18.4) * mm});
            skLineSegment(sketch, "E6.18.4.5", {"start": v(96.01, 25.1) * mm, "end": v(99.88, 25.1) * mm});
            skCircle(sketch, "E6.0.5.4", {"center": v(105.48, 17.4) * mm, "radius": 3.35 * mm});
            skLineSegment(sketch, "E6.2.5.4", {"start": v(101.61, 17.4) * mm, "end": v(103.55, 20.75) * mm});
            skLineSegment(sketch, "E6.5.5.4", {"start": v(107.42, 20.75) * mm, "end": v(109.35, 17.4) * mm});
            skLineSegment(sketch, "E6.8.5.4", {"start": v(109.35, 17.4) * mm, "end": v(107.42, 14.05) * mm});
            skPoint(sketch, "E6.11.5.4", {"position": v(105.48, 14.05) * mm});
            skLineSegment(sketch, "E6.12.5.4", {"start": v(103.55, 14.05) * mm, "end": v(101.61, 17.4) * mm});
            skLineSegment(sketch, "E6.15.5.4", {"start": v(107.42, 14.05) * mm, "end": v(103.55, 14.05) * mm});
            skLineSegment(sketch, "E6.18.5.4", {"start": v(103.55, 20.75) * mm, "end": v(107.42, 20.75) * mm});
            skCircle(sketch, "E6.0.5.5", {"center": v(113.02, 21.75) * mm, "radius": 3.35 * mm});
            skLineSegment(sketch, "E6.2.5.5", {"start": v(109.15, 21.75) * mm, "end": v(111.08, 25.1) * mm});
            skLineSegment(sketch, "E6.5.5.5", {"start": v(114.95, 25.1) * mm, "end": v(116.88, 21.75) * mm});
            skLineSegment(sketch, "E6.8.5.5", {"start": v(116.88, 21.75) * mm, "end": v(114.95, 18.4) * mm});
            skPoint(sketch, "E6.11.5.5", {"position": v(113.02, 18.4) * mm});
            skLineSegment(sketch, "E6.12.5.5", {"start": v(111.08, 18.4) * mm, "end": v(109.15, 21.75) * mm});
            skLineSegment(sketch, "E6.15.5.5", {"start": v(114.95, 18.4) * mm, "end": v(111.08, 18.4) * mm});
            skLineSegment(sketch, "E6.18.5.5", {"start": v(111.08, 25.1) * mm, "end": v(114.95, 25.1) * mm});
            skCircle(sketch, "E7.0.6.0", {"center": v(90.41, 0) * mm, "radius": 3.35 * mm});
            skLineSegment(sketch, "E7.2.6.0", {"start": v(86.54, 0) * mm, "end": v(88.48, 3.35) * mm});
            skLineSegment(sketch, "E7.5.6.0", {"start": v(92.35, 3.35) * mm, "end": v(94.28, 0) * mm});
            skLineSegment(sketch, "E7.8.6.0", {"start": v(94.28, 0) * mm, "end": v(92.35, -3.35) * mm});
            skPoint(sketch, "E7.11.6.0", {"position": v(90.41, -3.35) * mm});
            skLineSegment(sketch, "E7.12.6.0", {"start": v(88.48, -3.35) * mm, "end": v(86.54, 0) * mm});
            skLineSegment(sketch, "E7.15.6.0", {"start": v(92.35, -3.35) * mm, "end": v(88.48, -3.35) * mm});
            skLineSegment(sketch, "E7.18.6.0", {"start": v(88.48, 3.35) * mm, "end": v(92.35, 3.35) * mm});
            skCircle(sketch, "E7.0.6.1", {"center": v(97.95, 4.35) * mm, "radius": 3.35 * mm});
            skLineSegment(sketch, "E7.2.6.1", {"start": v(94.08, 4.35) * mm, "end": v(96.01, 7.7) * mm});
            skLineSegment(sketch, "E7.5.6.1", {"start": v(99.88, 7.7) * mm, "end": v(101.82, 4.35) * mm});
            skLineSegment(sketch, "E7.8.6.1", {"start": v(101.82, 4.35) * mm, "end": v(99.88, 1) * mm});
            skPoint(sketch, "E7.11.6.1", {"position": v(97.95, 1) * mm});
            skLineSegment(sketch, "E7.12.6.1", {"start": v(96.01, 1) * mm, "end": v(94.08, 4.35) * mm});
            skLineSegment(sketch, "E7.15.6.1", {"start": v(99.88, 1) * mm, "end": v(96.01, 1) * mm});
            skLineSegment(sketch, "E7.18.6.1", {"start": v(96.01, 7.7) * mm, "end": v(99.88, 7.7) * mm});
            skCircle(sketch, "E7.0.6.2", {"center": v(105.48, 8.7) * mm, "radius": 3.35 * mm});
            skLineSegment(sketch, "E7.2.6.2", {"start": v(101.61, 8.7) * mm, "end": v(103.55, 12.05) * mm});
            skLineSegment(sketch, "E7.5.6.2", {"start": v(107.42, 12.05) * mm, "end": v(109.35, 8.7) * mm});
            skLineSegment(sketch, "E7.8.6.2", {"start": v(109.35, 8.7) * mm, "end": v(107.42, 5.35) * mm});
            skPoint(sketch, "E7.11.6.2", {"position": v(105.48, 5.35) * mm});
            skLineSegment(sketch, "E7.12.6.2", {"start": v(103.55, 5.35) * mm, "end": v(101.61, 8.7) * mm});
            skLineSegment(sketch, "E7.15.6.2", {"start": v(107.42, 5.35) * mm, "end": v(103.55, 5.35) * mm});
            skLineSegment(sketch, "E7.18.6.2", {"start": v(103.55, 12.05) * mm, "end": v(107.42, 12.05) * mm});
            skCircle(sketch, "E7.0.6.3", {"center": v(113.02, 13.05) * mm, "radius": 3.35 * mm});
            skLineSegment(sketch, "E7.2.6.3", {"start": v(109.15, 13.05) * mm, "end": v(111.08, 16.4) * mm});
            skLineSegment(sketch, "E7.5.6.3", {"start": v(114.95, 16.4) * mm, "end": v(116.88, 13.05) * mm});
            skLineSegment(sketch, "E7.8.6.3", {"start": v(116.88, 13.05) * mm, "end": v(114.95, 9.7) * mm});
            skPoint(sketch, "E7.11.6.3", {"position": v(113.02, 9.7) * mm});
            skLineSegment(sketch, "E7.12.6.3", {"start": v(111.08, 9.7) * mm, "end": v(109.15, 13.05) * mm});
            skLineSegment(sketch, "E7.15.6.3", {"start": v(114.95, 9.7) * mm, "end": v(111.08, 9.7) * mm});
            skLineSegment(sketch, "E7.18.6.3", {"start": v(111.08, 16.4) * mm, "end": v(114.95, 16.4) * mm});
            skCircle(sketch, "E7.0.6.4", {"center": v(120.55, 17.4) * mm, "radius": 3.35 * mm, "construction": true});
            skLineSegment(sketch, "E7.2.6.4", {"start": v(116.68, 17.4) * mm, "end": v(118.62, 20.75) * mm, "construction": true});
            skLineSegment(sketch, "E7.5.6.4", {"start": v(122.48, 20.75) * mm, "end": v(124.42, 17.4) * mm, "construction": true});
            skLineSegment(sketch, "E7.8.6.4", {"start": v(124.42, 17.4) * mm, "end": v(122.48, 14.05) * mm, "construction": true});
            skPoint(sketch, "E7.11.6.4", {"position": v(120.55, 14.05) * mm});
            skLineSegment(sketch, "E7.12.6.4", {"start": v(118.62, 14.05) * mm, "end": v(116.68, 17.4) * mm, "construction": true});
            skLineSegment(sketch, "E7.15.6.4", {"start": v(122.48, 14.05) * mm, "end": v(118.62, 14.05) * mm, "construction": true});
            skLineSegment(sketch, "E7.18.6.4", {"start": v(118.62, 20.75) * mm, "end": v(122.48, 20.75) * mm, "construction": true});
            skCircle(sketch, "E7.0.6.5", {"center": v(128.09, 21.75) * mm, "radius": 3.35 * mm, "construction": true});
            skLineSegment(sketch, "E7.2.6.5", {"start": v(124.22, 21.75) * mm, "end": v(126.15, 25.1) * mm, "construction": true});
            skLineSegment(sketch, "E7.5.6.5", {"start": v(130.02, 25.1) * mm, "end": v(131.95, 21.75) * mm, "construction": true});
            skLineSegment(sketch, "E7.8.6.5", {"start": v(131.95, 21.75) * mm, "end": v(130.02, 18.4) * mm, "construction": true});
            skPoint(sketch, "E7.11.6.5", {"position": v(128.09, 18.4) * mm});
            skLineSegment(sketch, "E7.12.6.5", {"start": v(126.15, 18.4) * mm, "end": v(124.22, 21.75) * mm, "construction": true});
            skLineSegment(sketch, "E7.15.6.5", {"start": v(130.02, 18.4) * mm, "end": v(126.15, 18.4) * mm, "construction": true});
            skLineSegment(sketch, "E7.18.6.5", {"start": v(126.15, 25.1) * mm, "end": v(130.02, 25.1) * mm, "construction": true});
            skCircle(sketch, "E7.0.7.0", {"center": v(105.48, 0) * mm, "radius": 3.35 * mm});
            skLineSegment(sketch, "E7.2.7.0", {"start": v(101.61, 0) * mm, "end": v(103.55, 3.35) * mm});
            skLineSegment(sketch, "E7.5.7.0", {"start": v(107.42, 3.35) * mm, "end": v(109.35, 0) * mm});
            skLineSegment(sketch, "E7.8.7.0", {"start": v(109.35, 0) * mm, "end": v(107.42, -3.35) * mm});
            skPoint(sketch, "E7.11.7.0", {"position": v(105.48, -3.35) * mm});
            skLineSegment(sketch, "E7.12.7.0", {"start": v(103.55, -3.35) * mm, "end": v(101.61, 0) * mm});
            skLineSegment(sketch, "E7.15.7.0", {"start": v(107.42, -3.35) * mm, "end": v(103.55, -3.35) * mm});
            skLineSegment(sketch, "E7.18.7.0", {"start": v(103.55, 3.35) * mm, "end": v(107.42, 3.35) * mm});
            skCircle(sketch, "E7.0.7.1", {"center": v(113.02, 4.35) * mm, "radius": 3.35 * mm});
            skLineSegment(sketch, "E7.2.7.1", {"start": v(109.15, 4.35) * mm, "end": v(111.08, 7.7) * mm});
            skLineSegment(sketch, "E7.5.7.1", {"start": v(114.95, 7.7) * mm, "end": v(116.88, 4.35) * mm});
            skLineSegment(sketch, "E7.8.7.1", {"start": v(116.88, 4.35) * mm, "end": v(114.95, 1) * mm});
            skPoint(sketch, "E7.11.7.1", {"position": v(113.02, 1) * mm});
            skLineSegment(sketch, "E7.12.7.1", {"start": v(111.08, 1) * mm, "end": v(109.15, 4.35) * mm});
            skLineSegment(sketch, "E7.15.7.1", {"start": v(114.95, 1) * mm, "end": v(111.08, 1) * mm});
            skLineSegment(sketch, "E7.18.7.1", {"start": v(111.08, 7.7) * mm, "end": v(114.95, 7.7) * mm});
            skCircle(sketch, "E7.0.7.2", {"center": v(120.55, 8.7) * mm, "radius": 3.35 * mm, "construction": true});
            skLineSegment(sketch, "E7.2.7.2", {"start": v(116.68, 8.7) * mm, "end": v(118.62, 12.05) * mm, "construction": true});
            skLineSegment(sketch, "E7.5.7.2", {"start": v(122.48, 12.05) * mm, "end": v(124.42, 8.7) * mm, "construction": true});
            skLineSegment(sketch, "E7.8.7.2", {"start": v(124.42, 8.7) * mm, "end": v(122.48, 5.35) * mm, "construction": true});
            skPoint(sketch, "E7.11.7.2", {"position": v(120.55, 5.35) * mm});
            skLineSegment(sketch, "E7.12.7.2", {"start": v(118.62, 5.35) * mm, "end": v(116.68, 8.7) * mm, "construction": true});
            skLineSegment(sketch, "E7.15.7.2", {"start": v(122.48, 5.35) * mm, "end": v(118.62, 5.35) * mm, "construction": true});
            skLineSegment(sketch, "E7.18.7.2", {"start": v(118.62, 12.05) * mm, "end": v(122.48, 12.05) * mm, "construction": true});
            skCircle(sketch, "E7.0.7.3", {"center": v(128.09, 13.05) * mm, "radius": 3.35 * mm, "construction": true});
            skLineSegment(sketch, "E7.2.7.3", {"start": v(124.22, 13.05) * mm, "end": v(126.15, 16.4) * mm, "construction": true});
            skLineSegment(sketch, "E7.5.7.3", {"start": v(130.02, 16.4) * mm, "end": v(131.95, 13.05) * mm, "construction": true});
            skLineSegment(sketch, "E7.8.7.3", {"start": v(131.95, 13.05) * mm, "end": v(130.02, 9.7) * mm, "construction": true});
            skPoint(sketch, "E7.11.7.3", {"position": v(128.09, 9.7) * mm});
            skLineSegment(sketch, "E7.12.7.3", {"start": v(126.15, 9.7) * mm, "end": v(124.22, 13.05) * mm, "construction": true});
            skLineSegment(sketch, "E7.15.7.3", {"start": v(130.02, 9.7) * mm, "end": v(126.15, 9.7) * mm, "construction": true});
            skLineSegment(sketch, "E7.18.7.3", {"start": v(126.15, 16.4) * mm, "end": v(130.02, 16.4) * mm, "construction": true});
            skCircle(sketch, "E7.0.7.4", {"center": v(135.62, 17.4) * mm, "radius": 3.35 * mm, "construction": true});
            skLineSegment(sketch, "E7.2.7.4", {"start": v(131.75, 17.4) * mm, "end": v(133.69, 20.75) * mm, "construction": true});
            skLineSegment(sketch, "E7.5.7.4", {"start": v(137.55, 20.75) * mm, "end": v(139.49, 17.4) * mm, "construction": true});
            skLineSegment(sketch, "E7.8.7.4", {"start": v(139.49, 17.4) * mm, "end": v(137.55, 14.05) * mm, "construction": true});
            skPoint(sketch, "E7.11.7.4", {"position": v(135.62, 14.05) * mm});
            skLineSegment(sketch, "E7.12.7.4", {"start": v(133.69, 14.05) * mm, "end": v(131.75, 17.4) * mm, "construction": true});
            skLineSegment(sketch, "E7.15.7.4", {"start": v(137.55, 14.05) * mm, "end": v(133.69, 14.05) * mm, "construction": true});
            skLineSegment(sketch, "E7.18.7.4", {"start": v(133.69, 20.75) * mm, "end": v(137.55, 20.75) * mm, "construction": true});
            skCircle(sketch, "E7.0.7.5", {"center": v(143.15, 21.75) * mm, "radius": 3.35 * mm, "construction": true});
            skLineSegment(sketch, "E7.2.7.5", {"start": v(139.29, 21.75) * mm, "end": v(141.22, 25.1) * mm, "construction": true});
            skLineSegment(sketch, "E7.5.7.5", {"start": v(145.09, 25.1) * mm, "end": v(147.02, 21.75) * mm, "construction": true});
            skLineSegment(sketch, "E7.8.7.5", {"start": v(147.02, 21.75) * mm, "end": v(145.09, 18.4) * mm, "construction": true});
            skPoint(sketch, "E7.11.7.5", {"position": v(143.15, 18.4) * mm});
            skLineSegment(sketch, "E7.12.7.5", {"start": v(141.22, 18.4) * mm, "end": v(139.29, 21.75) * mm, "construction": true});
            skLineSegment(sketch, "E7.15.7.5", {"start": v(145.09, 18.4) * mm, "end": v(141.22, 18.4) * mm, "construction": true});
            skLineSegment(sketch, "E7.18.7.5", {"start": v(141.22, 25.1) * mm, "end": v(145.09, 25.1) * mm, "construction": true});
            skSolve(sketch);
        }
        {
            var Q0;
            Q0=qCreatedBy(makeId("Top.planeOp"),FACE);
            var sketch = newSketch(context, id + "F1", { "sketchPlane" : qUnion([Q0])});
            skLineSegment(sketch, "E8.bottom", {"start": v(23.27, 28.1) * mm, "end": v(119.88, 28.1) * mm});
            skLineSegment(sketch, "E8.top", {"start": v(23.27, -6.35) * mm, "end": v(119.88, -6.35) * mm});
            skLineSegment(sketch, "E8.left", {"start": v(23.27, 28.1) * mm, "end": v(23.27, -6.35) * mm});
            skLineSegment(sketch, "E8.right", {"start": v(119.88, 28.1) * mm, "end": v(119.88, -6.35) * mm});
            skSolve(sketch);
        }
        {
            var Q0;
            Q0 = qSketchRegion(id + "F1", true);
            extrude(context, id + "F2", {"entities" : qUnion([Q0]), "oppositeDirection" : true, "depth" : 11 * mm});
        }
        {
            var Q0;
            Q0 = qSketchRegion(id + "F0", true);
            extrude(context, id + "F3", {"entities" : qUnion([Q0]), "operationType" : NewBodyOperationType.REMOVE, "oppositeDirection" : true, "depth" : 8 * mm});
        }
        {
            var Q0;
            Q0=makeQuery(id+"F2.opExtrude","SWEPT_EDGE",EDGE,{"disambiguationData":[OSD([sQuery(id+"F1.wireOp",EDGE,"E8.top"),sQuery(id+"F1.wireOp",EDGE,"E8.left")])]});
            var Q1;
            Q1=makeQuery(id+"F2.opExtrude","SWEPT_EDGE",EDGE,{"disambiguationData":[OSD([sQuery(id+"F1.wireOp",EDGE,"E8.top"),sQuery(id+"F1.wireOp",EDGE,"E8.right")])]});
            fillet(context, id + "F4", {"entities" : qUnion([Q0, Q1]), "radius" : 6 * mm, "tangentPropagation" : true, "allowEdgeOverflow" : false});
        }
        {
            var Q0;
            Q0=makeQuery(id+"F2.opExtrude","CAP_EDGE",EDGE,{"disambiguationData":[OSD([sQuery(id+"F1.wireOp",EDGE,"E8.left")])],"isStart":false});
            var Q1;
            Q1=makeQuery(id+"F2.opExtrude","CAP_FACE",FACE,{"disambiguationData":[OSD([sQuery(id+"F1.wireOp",EDGE,"E8.bottom"),sQuery(id+"F1.wireOp",EDGE,"E8.top"),sQuery(id+"F1.wireOp",EDGE,"E8.left"),sQuery(id+"F1.wireOp",EDGE,"E8.right")])],"isStart":true});
            fillet(context, id + "F5", {"entities" : qUnion([Q0, Q1]), "radius" : 0.8 * mm, "tangentPropagation" : true, "allowEdgeOverflow" : false});
        }
        {
            var Q0;
            Q0=makeQuery(id+"F2.opExtrude","SWEPT_FACE",FACE,{"disambiguationData":[OSD([sQuery(id+"F1.wireOp",EDGE,"E8.bottom")])]});
            var sketch = newSketch(context, id + "F6", { "sketchPlane" : qUnion([Q0])});
            skLineSegment(sketch, "E9", {"start": v(-71.58, -0.8) * mm, "end": v(-71.58, -11) * mm, "construction": true});
            skLineSegment(sketch, "E10", {"start": v(-109.58, -5.9) * mm, "end": v(-33.58, -5.9) * mm, "construction": true});
            skPoint(sketch, "E10.startSnap0", {"position": v(-71.58, -5.9) * mm});
            skCircle(sketch, "E11", {"center": v(-109.58, -5.9) * mm, "radius": 2.4 * mm});
            skCircle(sketch, "E12", {"center": v(-33.58, -5.9) * mm, "radius": 2.4 * mm});
            skSolve(sketch);
        }
        {
            var Q0;
            Q0 = qSketchRegion(id + "F6", true);
            extrude(context, id + "F7", {"entities" : qUnion([Q0]), "operationType" : NewBodyOperationType.ADD, "depth" : 2 * mm});
        }
        {
            var Q0;
            Q0=makeQuery(id+"F7.opExtrude","CAP_FACE",FACE,{"disambiguationData":[OSD([sQuery(id+"F6.wireOp",EDGE,"E11")])],"isStart":false});
            var sketch = newSketch(context, id + "F8", { "sketchPlane" : qUnion([Q0])});
            skCircle(sketch, "E13", {"center": v(-109.58, -5.9) * mm, "radius": 4 * mm});
            skCircle(sketch, "E14.0", {"center": v(-33.58, -5.9) * mm, "radius": 2.4 * mm, "construction": true});
            skCircle(sketch, "E15", {"center": v(-33.58, -5.9) * mm, "radius": 4 * mm});
            skSolve(sketch);
        }
        {
            var Q0;
            Q0=makeQuery(id+"F8.imprint","IMPRINT",FACE,{"disambiguationData":[TD([[makeQuery(id+"F8.imprint","IMPRINT",EDGE,{"derivedFrom":sQuery(id+"F8.wireOp",EDGE,"E13")}),1.0]])]});
            var Q1;
            Q1=makeQuery(id+"F8.imprint","IMPRINT",FACE,{"disambiguationData":[TD([[makeQuery(id+"F8.imprint","IMPRINT",EDGE,{"derivedFrom":makeQuery(id+"F7.opExtrude","CAP_EDGE",EDGE,{"disambiguationData":[OSD([sQuery(id+"F6.wireOp",EDGE,"E11")])],"isStart":false})}),1.0]])]});
            var Q2;
            Q2=makeQuery(id+"F8.imprint","IMPRINT",FACE,{"disambiguationData":[TD([[makeQuery(id+"F8.imprint","IMPRINT",EDGE,{"derivedFrom":sQuery(id+"F8.wireOp",EDGE,"E15")}),1.0]])]});
            extrude(context, id + "F9", {"entities" : qUnion([Q0, Q1, Q2]), "operationType" : NewBodyOperationType.ADD, "depth" : 2 * mm});
        }
    });
